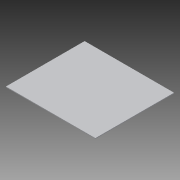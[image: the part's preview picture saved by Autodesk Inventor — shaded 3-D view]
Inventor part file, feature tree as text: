
AUTODESK INVENTOR PART (.ipt)
format: ipt  version: 2013 (Build 170138000, 138)  size: 64,000 bytes
history: native  units: mm
features: extrude x1, sketch x1
ambient origin geometry x8: Origin, YZ Plane, XZ Plane, XY Plane, X Axis, Y Axis, Z Axis, Center Point
bodies: Solid1 (feature_tree)
feature tree (2):
  extrude  "Extrusion1"  [1 undecoded]
  sketch  "Sketch1"  dims[d0=20.0mm d1=0.0mm]
note: 1 required parameter value undecoded (feature->parameter linkage not recoverable at this tier; creation-order binding heuristic only, values carry confidence <= 0.55)
